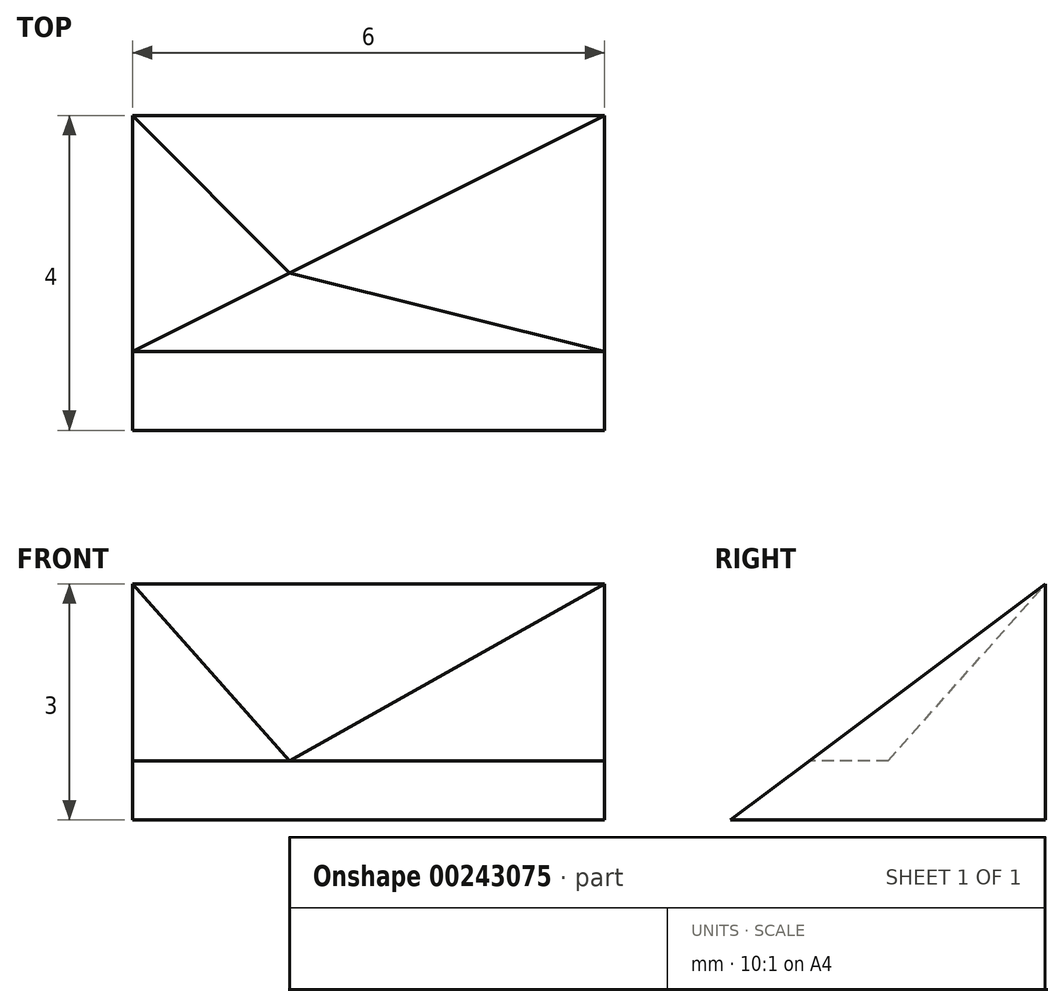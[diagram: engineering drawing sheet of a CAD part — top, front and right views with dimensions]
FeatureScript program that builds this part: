
annotation { "Feature Type Name" : "Feature", "Feature Type Description" : "" }
export const myFeature = defineFeature(function(context is Context, id is Id, definition is map)
    precondition{}
    {
        {
            var Q0;
            Q0=qCreatedBy(makeId("Right.planeOp"),FACE);
            var sketch = newSketch(context, id + "F0", { "sketchPlane" : qUnion([Q0])});
            skLineSegment(sketch, "E0", {"start": v(0, 0) * mm, "end": v(4, 0) * mm});
            skLineSegment(sketch, "E1", {"start": v(4, 0) * mm, "end": v(4, 3) * mm});
            skLineSegment(sketch, "E2", {"start": v(4, 3) * mm, "end": v(0, 0) * mm});
            skSolve(sketch);
        }
        {
            var Q0;
            Q0 = qSketchRegion(id + "F0", true);
            extrude(context, id + "F1", {"entities" : qUnion([Q0]), "depth" : 6 * mm});
        }
        {
            var Q0;
            Q0=qCreatedBy(makeId("Top.planeOp"),FACE);
            cPlane(context, id + "F2", {"entities" : qUnion([Q0]), "cplaneType" : CPlaneType.OFFSET, "offset" : 0.75 * mm, "width" : 150 * mm, "height" : 150 * mm});
        }
        {
            var Q0;
            Q0=qCreatedBy(id+"F2.planeOp",FACE);
            var sketch = newSketch(context, id + "F3", { "sketchPlane" : qUnion([Q0])});
            skLineSegment(sketch, "E3", {"start": v(0, 1) * mm, "end": v(6, 1) * mm});
            skLineSegment(sketch, "E4", {"start": v(2, 2) * mm, "end": v(0, 1) * mm});
            skLineSegment(sketch, "E5", {"start": v(6, 1) * mm, "end": v(2, 2) * mm});
            skSolve(sketch);
        }
        {
            var Q0;
            Q0 = qSketchRegion(id + "F3", true);
            extrude(context, id + "F4", {"entities" : qUnion([Q0]), "operationType" : NewBodyOperationType.REMOVE, "depth" : 25 * mm});
        }
        {
            var Q0;
            Q0=makeQuery(id+"F4.boolean.opBoolean","COPY",VERTEX,{"derivedFrom":makeQuery(id+"F4.opExtrude","CAP_VERTEX",VERTEX,{"disambiguationData":[OSD([sQuery(id+"F3.wireOp",EDGE,"E4"),sQuery(id+"F3.wireOp",EDGE,"E5")])],"isStart":true})});
            var Q1;
            Q1=makeQuery(id+"F4.boolean.opBoolean","COPY",VERTEX,{"derivedFrom":makeQuery(id+"F4.opExtrude","CAP_VERTEX",VERTEX,{"disambiguationData":[OSD([sQuery(id+"F3.wireOp",EDGE,"E3"),sQuery(id+"F3.wireOp",EDGE,"E5")])],"isStart":true})});
            var Q2;
            Q2=makeQuery(id+"F1.opExtrude","CAP_VERTEX",VERTEX,{"disambiguationData":[OSD([sQuery(id+"F0.wireOp",EDGE,"E1"),sQuery(id+"F0.wireOp",EDGE,"E2")])],"isStart":false});
            cPlane(context, id + "F5", {"entities" : qUnion([Q0, Q1, Q2]), "cplaneType" : CPlaneType.THREE_POINT, "offset" : 25 * mm, "width" : 150 * mm, "height" : 150 * mm});
        }
        {
            var Q0;
            Q0=qCreatedBy(id+"F5.planeOp",FACE);
            var sketch = newSketch(context, id + "F6", { "sketchPlane" : qUnion([Q0])});
            skPoint(sketch, "E6.0", {"position": v(1.89, -2.05) * mm});
            skPoint(sketch, "E6.1", {"position": v(5.93, -1.25) * mm});
            skPoint(sketch, "E6.2", {"position": v(5.93, -5) * mm});
            skLineSegment(sketch, "E7", {"start": v(1.89, -2.05) * mm, "end": v(5.93, -1.25) * mm});
            skLineSegment(sketch, "E8", {"start": v(5.93, -1.25) * mm, "end": v(6.7, -1) * mm});
            skLineSegment(sketch, "E9", {"start": v(6.7, -1) * mm, "end": v(5.93, -5) * mm});
            skLineSegment(sketch, "E10", {"start": v(1.89, -2.05) * mm, "end": v(5.93, -5) * mm});
            skSolve(sketch);
        }
        {
            var Q0;
            Q0 = qSketchRegion(id + "F6", true);
            extrude(context, id + "F7", {"entities" : qUnion([Q0]), "operationType" : NewBodyOperationType.REMOVE, "oppositeDirection" : true, "depth" : 25 * mm});
        }
        {
            var Q0;
            Q0=makeQuery(id+"F4.boolean.opBoolean","COPY",VERTEX,{"derivedFrom":makeQuery(id+"F4.opExtrude","CAP_VERTEX",VERTEX,{"disambiguationData":[OSD([sQuery(id+"F3.wireOp",EDGE,"E3"),sQuery(id+"F3.wireOp",EDGE,"E4")])],"isStart":true})});
            var Q1;
            Q1=makeQuery(id+"F7.boolean.opBoolean","MERGE",VERTEX,{"derivedFrom":[makeQuery(id+"F4.boolean.opBoolean","COPY",VERTEX,{"derivedFrom":makeQuery(id+"F4.opExtrude","CAP_VERTEX",VERTEX,{"disambiguationData":[OSD([sQuery(id+"F3.wireOp",EDGE,"E4"),sQuery(id+"F3.wireOp",EDGE,"E5")])],"isStart":true})}),makeQuery(id+"F7.opExtrude","CAP_VERTEX",VERTEX,{"disambiguationData":[OSD([sQuery(id+"F6.wireOp",EDGE,"E7"),sQuery(id+"F6.wireOp",EDGE,"E10")])],"isStart":true})]});
            var Q2;
            Q2=makeQuery(id+"F1.opExtrude","CAP_VERTEX",VERTEX,{"disambiguationData":[OSD([sQuery(id+"F0.wireOp",EDGE,"E1"),sQuery(id+"F0.wireOp",EDGE,"E2")])],"isStart":true});
            cPlane(context, id + "F8", {"entities" : qUnion([Q0, Q1, Q2]), "cplaneType" : CPlaneType.THREE_POINT, "offset" : 25 * mm, "width" : 150 * mm, "height" : 150 * mm});
        }
        {
            var Q0;
            Q0=qCreatedBy(id+"F8.planeOp",FACE);
            var sketch = newSketch(context, id + "F9", { "sketchPlane" : qUnion([Q0])});
            skPoint(sketch, "E11.0", {"position": v(0, -5) * mm});
            skPoint(sketch, "E11.1", {"position": v(0, -1.25) * mm});
            skPoint(sketch, "E11.2", {"position": v(2.09, -2.05) * mm});
            skLineSegment(sketch, "E12", {"start": v(0, -5) * mm, "end": v(0, -1.25) * mm});
            skLineSegment(sketch, "E13", {"start": v(2.09, -2.05) * mm, "end": v(0, -1.25) * mm});
            skLineSegment(sketch, "E14", {"start": v(2.09, -2.05) * mm, "end": v(0, -5) * mm});
            skSolve(sketch);
        }
        {
            var Q0;
            Q0 = qSketchRegion(id + "F9", true);
            extrude(context, id + "F10", {"entities" : qUnion([Q0]), "operationType" : NewBodyOperationType.REMOVE, "oppositeDirection" : true, "depth" : 25 * mm});
        }
        {
            var Q0;
            Q0=makeQuery(id+"F10.boolean.opBoolean","MERGE",VERTEX,{"derivedFrom":[makeQuery(id+"F1.opExtrude","CAP_VERTEX",VERTEX,{"disambiguationData":[OSD([sQuery(id+"F0.wireOp",EDGE,"E1"),sQuery(id+"F0.wireOp",EDGE,"E2")])],"isStart":true}),makeQuery(id+"F10.opExtrude","CAP_VERTEX",VERTEX,{"disambiguationData":[OSD([sQuery(id+"F9.wireOp",EDGE,"E12"),sQuery(id+"F9.wireOp",EDGE,"E14")])],"isStart":true})]});
            var Q1;
            Q1=makeQuery(id+"F10.boolean.opBoolean","MERGE",VERTEX,{"derivedFrom":[makeQuery(id+"F7.boolean.opBoolean","MERGE",VERTEX,{"derivedFrom":[makeQuery(id+"F4.boolean.opBoolean","COPY",VERTEX,{"derivedFrom":makeQuery(id+"F4.opExtrude","CAP_VERTEX",VERTEX,{"disambiguationData":[OSD([sQuery(id+"F3.wireOp",EDGE,"E4"),sQuery(id+"F3.wireOp",EDGE,"E5")])],"isStart":true})}),makeQuery(id+"F7.opExtrude","CAP_VERTEX",VERTEX,{"disambiguationData":[OSD([sQuery(id+"F6.wireOp",EDGE,"E7"),sQuery(id+"F6.wireOp",EDGE,"E10")])],"isStart":true})]}),makeQuery(id+"F10.opExtrude","CAP_VERTEX",VERTEX,{"disambiguationData":[OSD([sQuery(id+"F9.wireOp",EDGE,"E13"),sQuery(id+"F9.wireOp",EDGE,"E14")])],"isStart":true})]});
            var Q2;
            Q2=makeQuery(id+"F7.boolean.opBoolean","MERGE",VERTEX,{"derivedFrom":[makeQuery(id+"F1.opExtrude","CAP_VERTEX",VERTEX,{"disambiguationData":[OSD([sQuery(id+"F0.wireOp",EDGE,"E1"),sQuery(id+"F0.wireOp",EDGE,"E2")])],"isStart":false}),makeQuery(id+"F7.opExtrude","CAP_VERTEX",VERTEX,{"disambiguationData":[OSD([sQuery(id+"F6.wireOp",EDGE,"E9"),sQuery(id+"F6.wireOp",EDGE,"E10")])],"isStart":true})]});
            cPlane(context, id + "F11", {"entities" : qUnion([Q0, Q1, Q2]), "cplaneType" : CPlaneType.THREE_POINT, "offset" : 25 * mm, "width" : 150 * mm, "height" : 150 * mm});
        }
        {
            var Q0;
            Q0=qCreatedBy(id+"F11.planeOp",FACE);
            var sketch = newSketch(context, id + "F12", { "sketchPlane" : qUnion([Q0])});
            skPoint(sketch, "E15.0", {"position": v(0, 4.9) * mm});
            skPoint(sketch, "E15.1", {"position": v(-2, 1.89) * mm});
            skPoint(sketch, "E15.2", {"position": v(-6, 4.9) * mm});
            skLineSegment(sketch, "E16", {"start": v(0, 4.9) * mm, "end": v(-2, 1.89) * mm});
            skLineSegment(sketch, "E17", {"start": v(-6, 4.9) * mm, "end": v(-2, 1.89) * mm});
            skLineSegment(sketch, "E18", {"start": v(0, 4.9) * mm, "end": v(-6, 4.9) * mm});
            skSolve(sketch);
        }
        {
            var Q0;
            Q0 = qSketchRegion(id + "F12", true);
            extrude(context, id + "F13", {"entities" : qUnion([Q0]), "operationType" : NewBodyOperationType.REMOVE, "oppositeDirection" : true, "depth" : 25 * mm});
        }
    });
